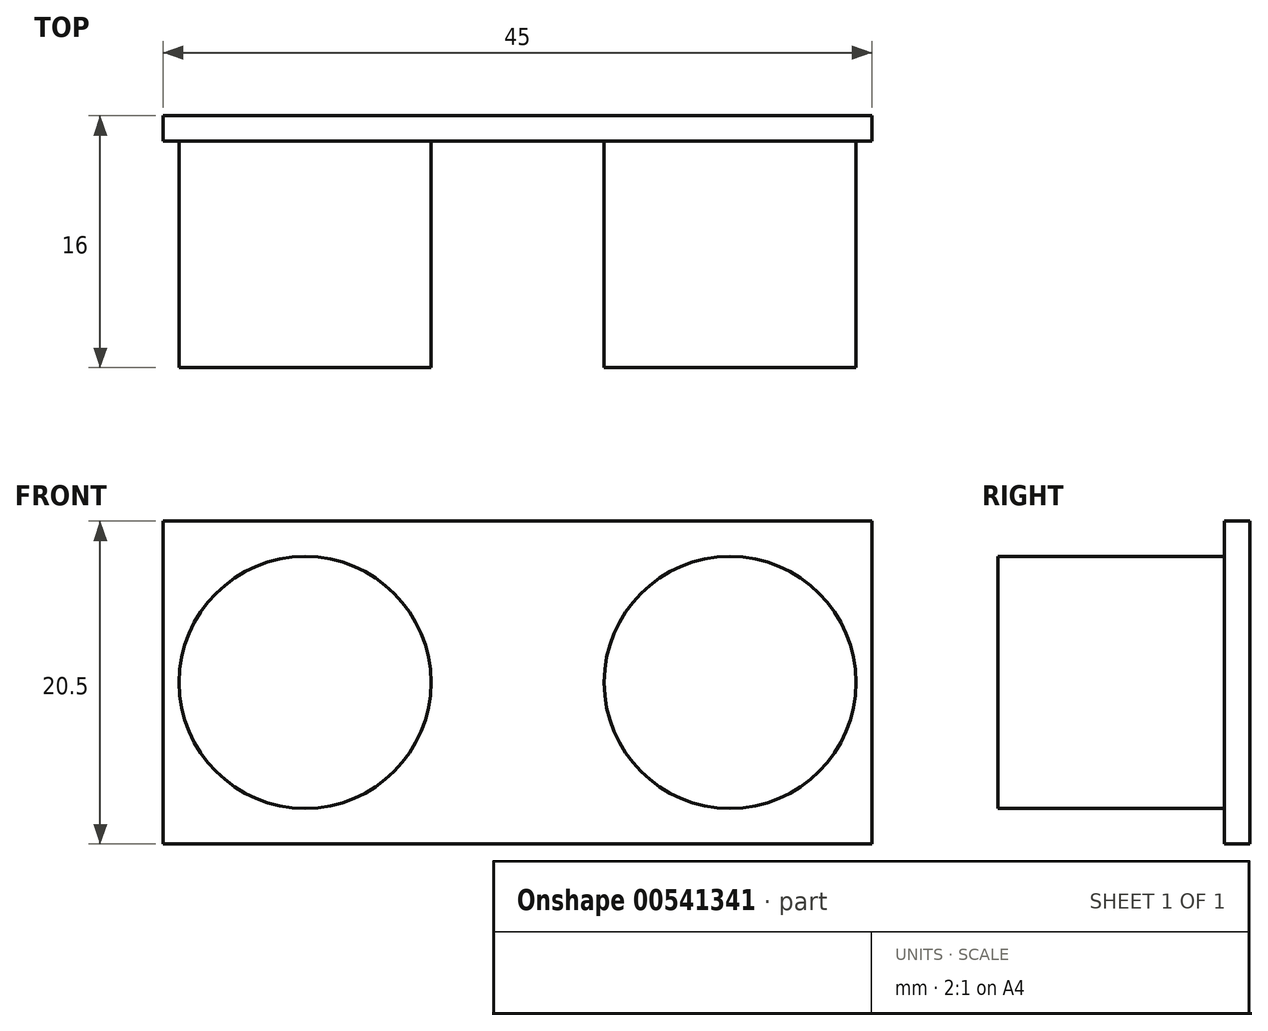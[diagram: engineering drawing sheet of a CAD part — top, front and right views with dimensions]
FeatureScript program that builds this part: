
annotation { "Feature Type Name" : "Feature", "Feature Type Description" : "" }
export const myFeature = defineFeature(function(context is Context, id is Id, definition is map)
    precondition{}
    {
        {
            var Q0;
            Q0=qCreatedBy(makeId("Front.planeOp"),FACE);
            var sketch = newSketch(context, id + "F0", { "sketchPlane" : qUnion([Q0])});
            skLineSegment(sketch, "E0.bottom", {"start": v(22.5, 10.25) * mm, "end": v(-22.5, 10.25) * mm});
            skLineSegment(sketch, "E0.top", {"start": v(22.5, -10.25) * mm, "end": v(-22.5, -10.25) * mm});
            skLineSegment(sketch, "E0.left", {"start": v(22.5, 10.25) * mm, "end": v(22.5, -10.25) * mm});
            skLineSegment(sketch, "E0.right", {"start": v(-22.5, 10.25) * mm, "end": v(-22.5, -10.25) * mm});
            skPoint(sketch, "E0.middle", {"position": v(0, 0) * mm});
            skSolve(sketch);
        }
        {
            var Q0;
            Q0=makeQuery(id+"F0.imprint","IMPRINT",FACE,{"disambiguationData":[TD([[makeQuery(id+"F0.imprint","IMPRINT",EDGE,{"derivedFrom":sQuery(id+"F0.wireOp",EDGE,"E0.bottom")}),1.0]])]});
            extrude(context, id + "F1", {"entities" : qUnion([Q0]), "depth" : 1.6 * mm, "offsetDistance" : 25.4 * mm});
        }
        {
            var Q0;
            Q0=qCreatedBy(makeId("Front.planeOp"),FACE);
            var sketch = newSketch(context, id + "F2", { "sketchPlane" : qUnion([Q0])});
            skCircle(sketch, "E1", {"center": v(-13.5, 0) * mm, "radius": 8 * mm});
            skCircle(sketch, "E2", {"center": v(13.5, 0) * mm, "radius": 8 * mm});
            skLineSegment(sketch, "E3", {"start": v(0, 11.13) * mm, "end": v(0, -10.53) * mm});
            skLineSegment(sketch, "E4", {"start": v(0, -10.53) * mm, "end": v(0, 0) * mm});
            skLineSegment(sketch, "E5", {"start": v(0, 0) * mm, "end": v(5.5, 0) * mm});
            skLineSegment(sketch, "E6", {"start": v(5.5, 0) * mm, "end": v(-5.5, 0) * mm});
            skPoint(sketch, "E7", {"position": v(0, 0) * mm});
            skSolve(sketch);
        }
        {
            var Q0;
            Q0=makeQuery(id+"F2.imprint","IMPRINT",FACE,{"disambiguationData":[TD([[makeQuery(id+"F2.imprint","IMPRINT",EDGE,{"derivedFrom":sQuery(id+"F2.wireOp",EDGE,"E1")}),1.0]])]});
            var Q1;
            Q1=makeQuery(id+"F2.imprint","IMPRINT",FACE,{"disambiguationData":[TD([[makeQuery(id+"F2.imprint","IMPRINT",EDGE,{"derivedFrom":sQuery(id+"F2.wireOp",EDGE,"E2")}),1.0]])]});
            extrude(context, id + "F3", {"entities" : qUnion([Q0, Q1]), "operationType" : NewBodyOperationType.ADD, "depth" : 16 * mm, "offsetDistance" : 25.4 * mm});
        }
    });
